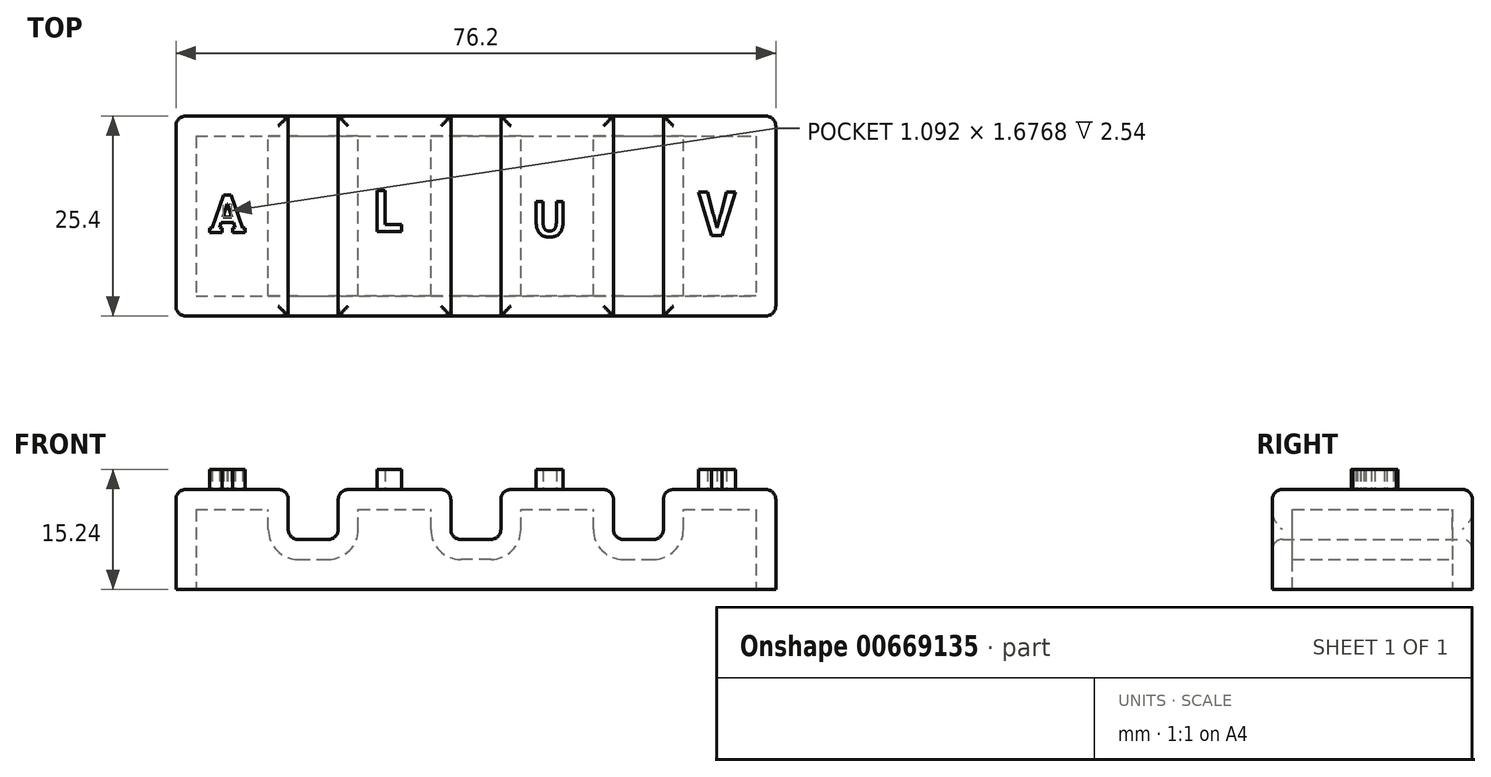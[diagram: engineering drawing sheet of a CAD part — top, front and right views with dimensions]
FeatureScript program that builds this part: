
annotation { "Feature Type Name" : "Feature", "Feature Type Description" : "" }
export const myFeature = defineFeature(function(context is Context, id is Id, definition is map)
    precondition{}
    {
        {
            var Q0;
            Q0=qCreatedBy(makeId("Top.planeOp"),FACE);
            var sketch = newSketch(context, id + "F0", { "sketchPlane" : qUnion([Q0])});
            skLineSegment(sketch, "E0.bottom", {"start": v(-38.1, 12.7) * mm, "end": v(38.1, 12.7) * mm});
            skLineSegment(sketch, "E0.top", {"start": v(-38.1, -12.7) * mm, "end": v(38.1, -12.7) * mm});
            skLineSegment(sketch, "E0.left", {"start": v(-38.1, 12.7) * mm, "end": v(-38.1, -12.7) * mm});
            skLineSegment(sketch, "E0.right", {"start": v(38.1, 12.7) * mm, "end": v(38.1, -12.7) * mm});
            skPoint(sketch, "E0.middle", {"position": v(0, 0) * mm});
            skSolve(sketch);
        }
        {
            var Q0;
            Q0 = qSketchRegion(id + "F0", true);
            extrude(context, id + "F1", {"entities" : qUnion([Q0]), "depth" : 12.7 * mm, "offsetDistance" : 25.4 * mm});
        }
        {
            var Q0;
            Q0=makeQuery(id+"F1.opExtrude","SWEPT_FACE",FACE,{"disambiguationData":[OSD([sQuery(id+"F0.wireOp",EDGE,"E0.bottom")])]});
            var sketch = newSketch(context, id + "F2", { "sketchPlane" : qUnion([Q0])});
            skLineSegment(sketch, "E1", {"start": v(-38.1, 6.35) * mm, "end": v(38.1, 6.35) * mm, "construction": true});
            skLineSegment(sketch, "E2.bottom", {"start": v(3.18, 6.35) * mm, "end": v(-3.17, 6.35) * mm});
            skLineSegment(sketch, "E2.top", {"start": v(3.18, 19.05) * mm, "end": v(-3.18, 19.05) * mm});
            skLineSegment(sketch, "E2.left", {"start": v(3.18, 6.35) * mm, "end": v(3.17, 19.05) * mm});
            skLineSegment(sketch, "E2.right", {"start": v(-3.17, 6.35) * mm, "end": v(-3.18, 19.05) * mm});
            skPoint(sketch, "E2.middle", {"position": v(0, 12.7) * mm});
            skLineSegment(sketch, "E3.bottom", {"start": v(17.48, 6.35) * mm, "end": v(23.83, 6.35) * mm});
            skLineSegment(sketch, "E3.top", {"start": v(17.48, 19.05) * mm, "end": v(23.83, 19.05) * mm});
            skLineSegment(sketch, "E3.left", {"start": v(17.48, 6.35) * mm, "end": v(17.48, 19.05) * mm});
            skLineSegment(sketch, "E3.right", {"start": v(23.83, 6.35) * mm, "end": v(23.83, 19.05) * mm});
            skPoint(sketch, "E3.middle", {"position": v(20.65, 12.7) * mm});
            skLineSegment(sketch, "E4.bottom", {"start": v(-23.83, 6.35) * mm, "end": v(-17.48, 6.35) * mm});
            skLineSegment(sketch, "E4.top", {"start": v(-23.83, 19.05) * mm, "end": v(-17.48, 19.05) * mm});
            skLineSegment(sketch, "E4.left", {"start": v(-23.83, 6.35) * mm, "end": v(-23.83, 19.05) * mm});
            skLineSegment(sketch, "E4.right", {"start": v(-17.48, 6.35) * mm, "end": v(-17.48, 19.05) * mm});
            skPoint(sketch, "E4.middle", {"position": v(-20.65, 12.7) * mm});
            skSolve(sketch);
        }
        {
            var Q0;
            Q0 = qSketchRegion(id + "F2", true);
            extrude(context, id + "F3", {"entities" : qUnion([Q0]), "operationType" : NewBodyOperationType.REMOVE, "endBound" : BoundingType.THROUGH_ALL, "oppositeDirection" : true, "depth" : 25.4 * mm, "offsetDistance" : 25.4 * mm});
        }
        {
            var Q0;
            {var subQ0=sQuery(id+"F0.wireOp",EDGE,"E0.bottom");var subQ1=sQuery(id+"F0.wireOp",EDGE,"E0.right");var subQ2=sQuery(id+"F0.wireOp",EDGE,"E0.top");Q0=makeQuery(id+"F3.boolean.opBoolean","SPLIT",FACE,{"disambiguationData":[TD([makeQuery(id+"F1.opExtrude","SWEPT_FACE",FACE,{"disambiguationData":[OSD([subQ1])]})])],"derivedFrom":makeQuery(id+"F1.opExtrude","CAP_FACE",FACE,{"disambiguationData":[OSD([subQ0,subQ2,sQuery(id+"F0.wireOp",EDGE,"E0.left"),subQ1])],"isStart":false})});}
            var Q1;
            {var subQ0=sQuery(id+"F0.wireOp",EDGE,"E0.bottom");var subQ1=sQuery(id+"F0.wireOp",EDGE,"E0.top");Q1=makeQuery(id+"F3.boolean.opBoolean","SPLIT",FACE,{"disambiguationData":[TD([makeQuery(id+"F3.opExtrude","SWEPT_FACE",FACE,{"disambiguationData":[OSD([sQuery(id+"F2.wireOp",EDGE,"E2.left")])]})])],"derivedFrom":makeQuery(id+"F1.opExtrude","CAP_FACE",FACE,{"disambiguationData":[OSD([subQ0,subQ1,sQuery(id+"F0.wireOp",EDGE,"E0.left"),sQuery(id+"F0.wireOp",EDGE,"E0.right")])],"isStart":false})});}
            var Q2;
            {var subQ0=sQuery(id+"F0.wireOp",EDGE,"E0.bottom");var subQ1=sQuery(id+"F0.wireOp",EDGE,"E0.top");var subQ2=sQuery(id+"F0.wireOp",EDGE,"E0.left");Q2=makeQuery(id+"F3.boolean.opBoolean","SPLIT",FACE,{"disambiguationData":[TD([makeQuery(id+"F1.opExtrude","SWEPT_FACE",FACE,{"disambiguationData":[OSD([subQ2])]})])],"derivedFrom":makeQuery(id+"F1.opExtrude","CAP_FACE",FACE,{"disambiguationData":[OSD([subQ0,subQ1,subQ2,sQuery(id+"F0.wireOp",EDGE,"E0.right")])],"isStart":false})});}
            var Q3;
            {var subQ0=sQuery(id+"F0.wireOp",EDGE,"E0.bottom");var subQ1=sQuery(id+"F0.wireOp",EDGE,"E0.top");Q3=makeQuery(id+"F3.boolean.opBoolean","SPLIT",FACE,{"disambiguationData":[TD([makeQuery(id+"F3.opExtrude","SWEPT_FACE",FACE,{"disambiguationData":[OSD([sQuery(id+"F2.wireOp",EDGE,"E2.right")])]})])],"derivedFrom":makeQuery(id+"F1.opExtrude","CAP_FACE",FACE,{"disambiguationData":[OSD([subQ0,subQ1,sQuery(id+"F0.wireOp",EDGE,"E0.left"),sQuery(id+"F0.wireOp",EDGE,"E0.right")])],"isStart":false})});}
            var Q4;
            Q4=makeQuery(id+"F3.boolean.opBoolean","COPY",FACE,{"derivedFrom":makeQuery(id+"F3.opExtrude","SWEPT_FACE",FACE,{"disambiguationData":[OSD([sQuery(id+"F2.wireOp",EDGE,"E4.bottom")])]})});
            var Q5;
            Q5=makeQuery(id+"F3.boolean.opBoolean","COPY",FACE,{"derivedFrom":makeQuery(id+"F3.opExtrude","SWEPT_FACE",FACE,{"disambiguationData":[OSD([sQuery(id+"F2.wireOp",EDGE,"E2.bottom")])]})});
            var Q6;
            Q6=makeQuery(id+"F3.boolean.opBoolean","COPY",FACE,{"derivedFrom":makeQuery(id+"F3.opExtrude","SWEPT_FACE",FACE,{"disambiguationData":[OSD([sQuery(id+"F2.wireOp",EDGE,"E3.bottom")])]})});
            var Q7;
            Q7=makeQuery(id+"F1.opExtrude","SWEPT_EDGE",EDGE,{"disambiguationData":[OSD([sQuery(id+"F0.wireOp",EDGE,"E0.bottom"),sQuery(id+"F0.wireOp",EDGE,"E0.left")])]});
            var Q8;
            Q8=makeQuery(id+"F1.opExtrude","SWEPT_EDGE",EDGE,{"disambiguationData":[OSD([sQuery(id+"F0.wireOp",EDGE,"E0.top"),sQuery(id+"F0.wireOp",EDGE,"E0.left")])]});
            var Q9;
            Q9=makeQuery(id+"F1.opExtrude","SWEPT_EDGE",EDGE,{"disambiguationData":[OSD([sQuery(id+"F0.wireOp",EDGE,"E0.bottom"),sQuery(id+"F0.wireOp",EDGE,"E0.right")])]});
            var Q10;
            Q10=makeQuery(id+"F1.opExtrude","SWEPT_EDGE",EDGE,{"disambiguationData":[OSD([sQuery(id+"F0.wireOp",EDGE,"E0.top"),sQuery(id+"F0.wireOp",EDGE,"E0.right")])]});
            fillet(context, id + "F4", {"entities" : qUnion([Q0, Q1, Q2, Q3, Q4, Q5, Q6, Q7, Q8, Q9, Q10]), "radius" : 1.27 * mm, "tangentPropagation" : true, "allowEdgeOverflow" : false});
        }
        {
            var Q0;
            Q0=makeQuery(id+"F1.opExtrude","CAP_FACE",FACE,{"disambiguationData":[OSD([sQuery(id+"F0.wireOp",EDGE,"E0.bottom"),sQuery(id+"F0.wireOp",EDGE,"E0.top"),sQuery(id+"F0.wireOp",EDGE,"E0.left"),sQuery(id+"F0.wireOp",EDGE,"E0.right")])],"isStart":true});
            shell(context, id + "F5", {"entities" : qUnion([Q0]), "thickness" : 2.54 * mm});
        }
        {
            var Q0;
            {var subQ0=sQuery(id+"F0.wireOp",EDGE,"E0.bottom");var subQ1=sQuery(id+"F0.wireOp",EDGE,"E0.top");var subQ2=sQuery(id+"F0.wireOp",EDGE,"E0.left");Q0=makeQuery(id+"F3.boolean.opBoolean","SPLIT",FACE,{"disambiguationData":[TD([makeQuery(id+"F1.opExtrude","SWEPT_FACE",FACE,{"disambiguationData":[OSD([subQ2])]})])],"derivedFrom":makeQuery(id+"F1.opExtrude","CAP_FACE",FACE,{"disambiguationData":[OSD([subQ0,subQ1,subQ2,sQuery(id+"F0.wireOp",EDGE,"E0.right")])],"isStart":false})});}
            var sketch = newSketch(context, id + "F6", { "sketchPlane" : qUnion([Q0])});
            skText(sketch, "E5", { "text": "A\n\n\n", "fontName": "RobotoSlab-Bold.ttf"});
            const initialGuessF6  = {"E5": [-0.03397, -0.00212, 1, 0, 0.00482]};
            skSetInitialGuess(sketch, initialGuessF6);
            skSolve(sketch);
        }
        {
            var Q0;
            Q0 = qSketchRegion(id + "F6", true);
            extrude(context, id + "F7", {"entities" : qUnion([Q0]), "operationType" : NewBodyOperationType.ADD, "depth" : 2.54 * mm, "offsetDistance" : 25.4 * mm});
        }
        {
            var Q0;
            {var subQ0=sQuery(id+"F0.wireOp",EDGE,"E0.bottom");var subQ1=sQuery(id+"F0.wireOp",EDGE,"E0.top");Q0=makeQuery(id+"F3.boolean.opBoolean","SPLIT",FACE,{"disambiguationData":[TD([makeQuery(id+"F3.opExtrude","SWEPT_FACE",FACE,{"disambiguationData":[OSD([sQuery(id+"F2.wireOp",EDGE,"E2.left")])]})])],"derivedFrom":makeQuery(id+"F1.opExtrude","CAP_FACE",FACE,{"disambiguationData":[OSD([subQ0,subQ1,sQuery(id+"F0.wireOp",EDGE,"E0.left"),sQuery(id+"F0.wireOp",EDGE,"E0.right")])],"isStart":false})});}
            var sketch = newSketch(context, id + "F8", { "sketchPlane" : qUnion([Q0])});
            skText(sketch, "E6", { "text": "L\n", "fontName": "NotoSansCJKkr-Bold.otf"});
            const initialGuessF8  = {"E6": [-0.01318, -0.00196, 1, 0, 0.00505]};
            skSetInitialGuess(sketch, initialGuessF8);
            skSolve(sketch);
        }
        {
            var Q0;
            Q0 = qSketchRegion(id + "F8", true);
            extrude(context, id + "F9", {"entities" : qUnion([Q0]), "operationType" : NewBodyOperationType.ADD, "depth" : 2.54 * mm, "offsetDistance" : 25.4 * mm});
        }
        {
            var Q0;
            {var subQ0=sQuery(id+"F0.wireOp",EDGE,"E0.bottom");var subQ1=sQuery(id+"F0.wireOp",EDGE,"E0.top");Q0=makeQuery(id+"F3.boolean.opBoolean","SPLIT",FACE,{"disambiguationData":[TD([makeQuery(id+"F3.opExtrude","SWEPT_FACE",FACE,{"disambiguationData":[OSD([sQuery(id+"F2.wireOp",EDGE,"E2.right")])]})])],"derivedFrom":makeQuery(id+"F1.opExtrude","CAP_FACE",FACE,{"disambiguationData":[OSD([subQ0,subQ1,sQuery(id+"F0.wireOp",EDGE,"E0.left"),sQuery(id+"F0.wireOp",EDGE,"E0.right")])],"isStart":false})});}
            var sketch = newSketch(context, id + "F10", { "sketchPlane" : qUnion([Q0])});
            skText(sketch, "E7", { "text": "U", "fontName": "NotoSansCJKkr-Bold.otf"});
            const initialGuessF10  = {"E7": [0.00713, -0.0026, 1, 0, 0.0043]};
            skSetInitialGuess(sketch, initialGuessF10);
            skSolve(sketch);
        }
        {
            var Q0;
            Q0 = qSketchRegion(id + "F10", true);
            var Q1;
            Q1 = qSketchRegion(id + "F12", true);
            extrude(context, id + "F11", {"entities" : qUnion([Q0, Q1]), "operationType" : NewBodyOperationType.ADD, "depth" : 2.54 * mm, "offsetDistance" : 25.4 * mm});
        }
        {
            var Q0;
            {var subQ0=sQuery(id+"F0.wireOp",EDGE,"E0.bottom");var subQ1=sQuery(id+"F0.wireOp",EDGE,"E0.right");var subQ2=sQuery(id+"F0.wireOp",EDGE,"E0.top");Q0=makeQuery(id+"F3.boolean.opBoolean","SPLIT",FACE,{"disambiguationData":[TD([makeQuery(id+"F1.opExtrude","SWEPT_FACE",FACE,{"disambiguationData":[OSD([subQ1])]})])],"derivedFrom":makeQuery(id+"F1.opExtrude","CAP_FACE",FACE,{"disambiguationData":[OSD([subQ0,subQ2,sQuery(id+"F0.wireOp",EDGE,"E0.left"),subQ1])],"isStart":false})});}
            var sketch = newSketch(context, id + "F12", { "sketchPlane" : qUnion([Q0])});
            skSolve(sketch);
        }
        {
            var Q0;
            {var subQ0=sQuery(id+"F0.wireOp",EDGE,"E0.bottom");var subQ2=sQuery(id+"F0.wireOp",EDGE,"E0.right");var subQ3=makeQuery(id+"F1.opExtrude","SWEPT_FACE",FACE,{"disambiguationData":[OSD([subQ2])]});var subQ5=sQuery(id+"F0.wireOp",EDGE,"E0.top");var subQ7=makeQuery(id+"F1.opExtrude","CAP_FACE",FACE,{"disambiguationData":[OSD([subQ0,subQ5,sQuery(id+"F0.wireOp",EDGE,"E0.left"),subQ2])],"isStart":false});var subQ8=makeQuery(id+"F3.boolean.opBoolean","SPLIT",FACE,{"disambiguationData":[TD([subQ3])],"derivedFrom":subQ7});Q0=makeQuery(id+"F12.imprint","IMPRINT",FACE,{"disambiguationData":[TD([[makeQuery(id+"F12.imprint","IMPRINT",EDGE,{"derivedFrom":makeQuery(id+"F4.opFillet","BLEND_EDGE",EDGE,{"blendedFrom":[makeQuery(id+"F1.opExtrude","CAP_EDGE",EDGE,{"disambiguationData":[OSD([subQ2])],"isStart":false}),subQ8],"blendedInto":[subQ8]})}),1.0]])]});}
            var sketch = newSketch(context, id + "F13", { "sketchPlane" : qUnion([Q0])});
            skText(sketch, "E8", { "text": "V", "fontName": "NotoSansCJKkr-Bold.otf"});
            const initialGuessF13  = {"E8": [0.0283, -0.0025, 1, 0, 0.00538]};
            skSetInitialGuess(sketch, initialGuessF13);
            skSolve(sketch);
        }
        {
            var Q0;
            Q0 = qSketchRegion(id + "F13", true);
            var Q1;
            Q1=makeQuery(id+"Faco6RoFqaBPnlx_1.opExtrude","CAP_FACE",FACE,{"disambiguationData":[OSD([sQuery(id+"F0.wireOp",EDGE,"E0.bottom"),sQuery(id+"F0.wireOp",EDGE,"E0.top"),sQuery(id+"F0.wireOp",EDGE,"E0.left"),sQuery(id+"F0.wireOp",EDGE,"E0.right"),sQuery(id+"F2.wireOp",EDGE,"E2.right"),sQuery(id+"F2.wireOp",EDGE,"E4.right")])],"isStart":false});
            extrude(context, id + "F14", {"entities" : qUnion([Q0, Q1]), "operationType" : NewBodyOperationType.ADD, "depth" : 2.54 * mm, "offsetDistance" : 25.4 * mm});
        }
    });
